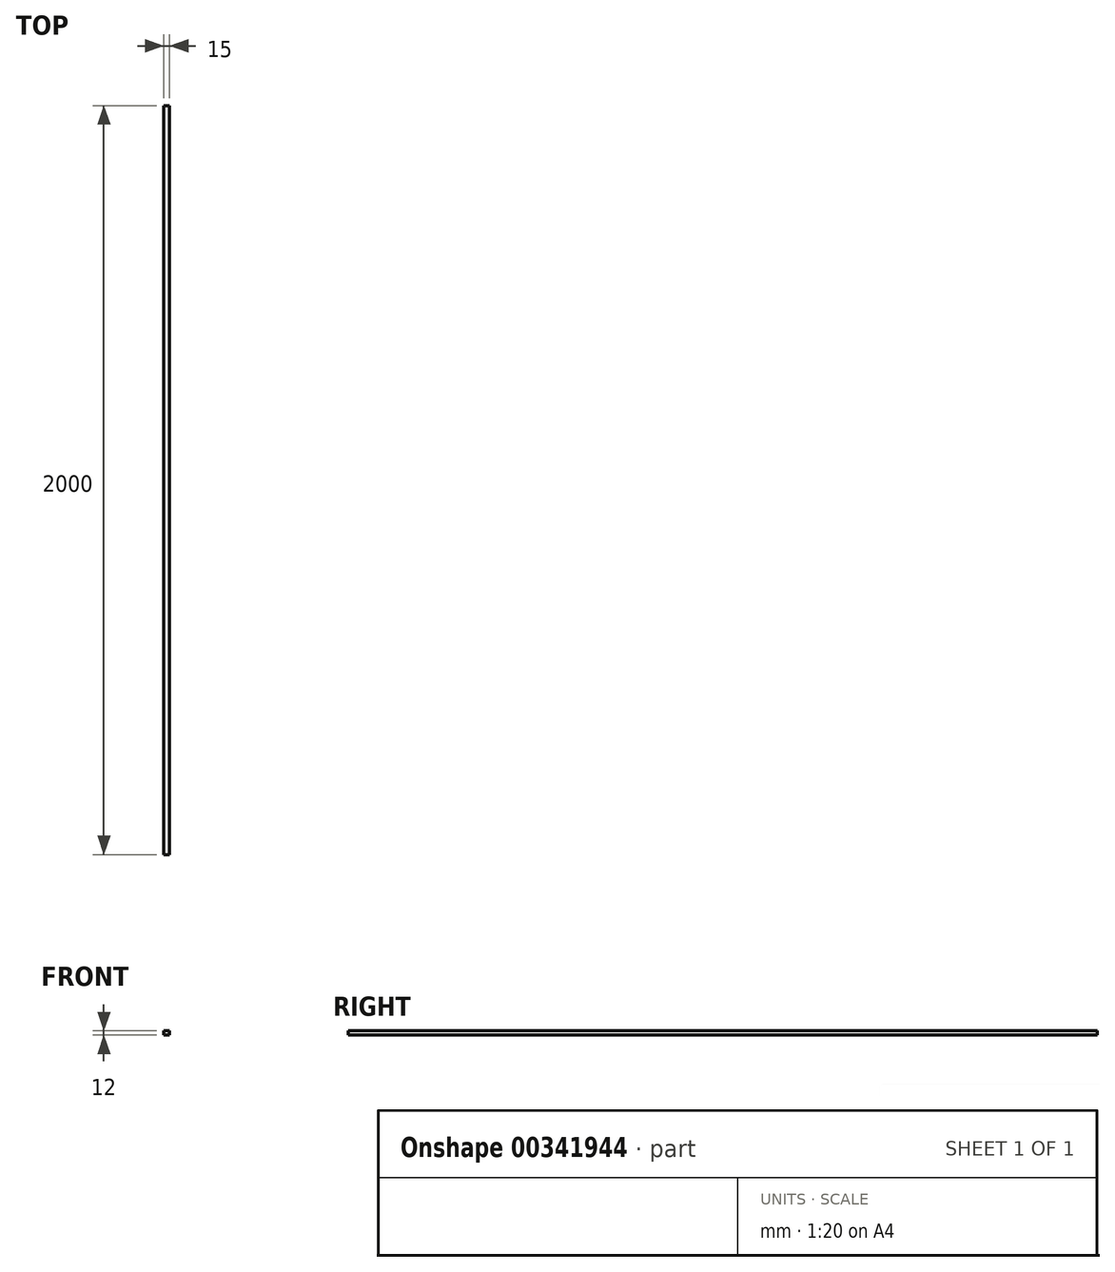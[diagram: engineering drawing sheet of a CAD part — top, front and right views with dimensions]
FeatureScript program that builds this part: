
annotation { "Feature Type Name" : "Feature", "Feature Type Description" : "" }
export const myFeature = defineFeature(function(context is Context, id is Id, definition is map)
    precondition{}
    {
        {
            var Q0;
            Q0=qCreatedBy(makeId("Front.planeOp"),FACE);
            var sketch = newSketch(context, id + "F0", { "sketchPlane" : qUnion([Q0])});
            skLineSegment(sketch, "E0.bottom", {"start": v(-7.5, 6) * mm, "end": v(7.5, 6) * mm});
            skLineSegment(sketch, "E0.top", {"start": v(-7.5, -6) * mm, "end": v(7.5, -6) * mm});
            skLineSegment(sketch, "E0.left", {"start": v(-7.5, 6) * mm, "end": v(-7.5, -6) * mm});
            skLineSegment(sketch, "E0.right", {"start": v(7.5, 6) * mm, "end": v(7.5, -6) * mm});
            skPoint(sketch, "E0.middle", {"position": v(0, 0) * mm});
            skSolve(sketch);
        }
        {
            var Q0;
            Q0 = qSketchRegion(id + "F0", true);
            extrude(context, id + "F1", {"entities" : qUnion([Q0]), "depth" : 1000 * mm, "hasSecondDirection" : true, "secondDirectionOppositeDirection" : true, "secondDirectionDepth" : 1000 * mm});
        }
    });
